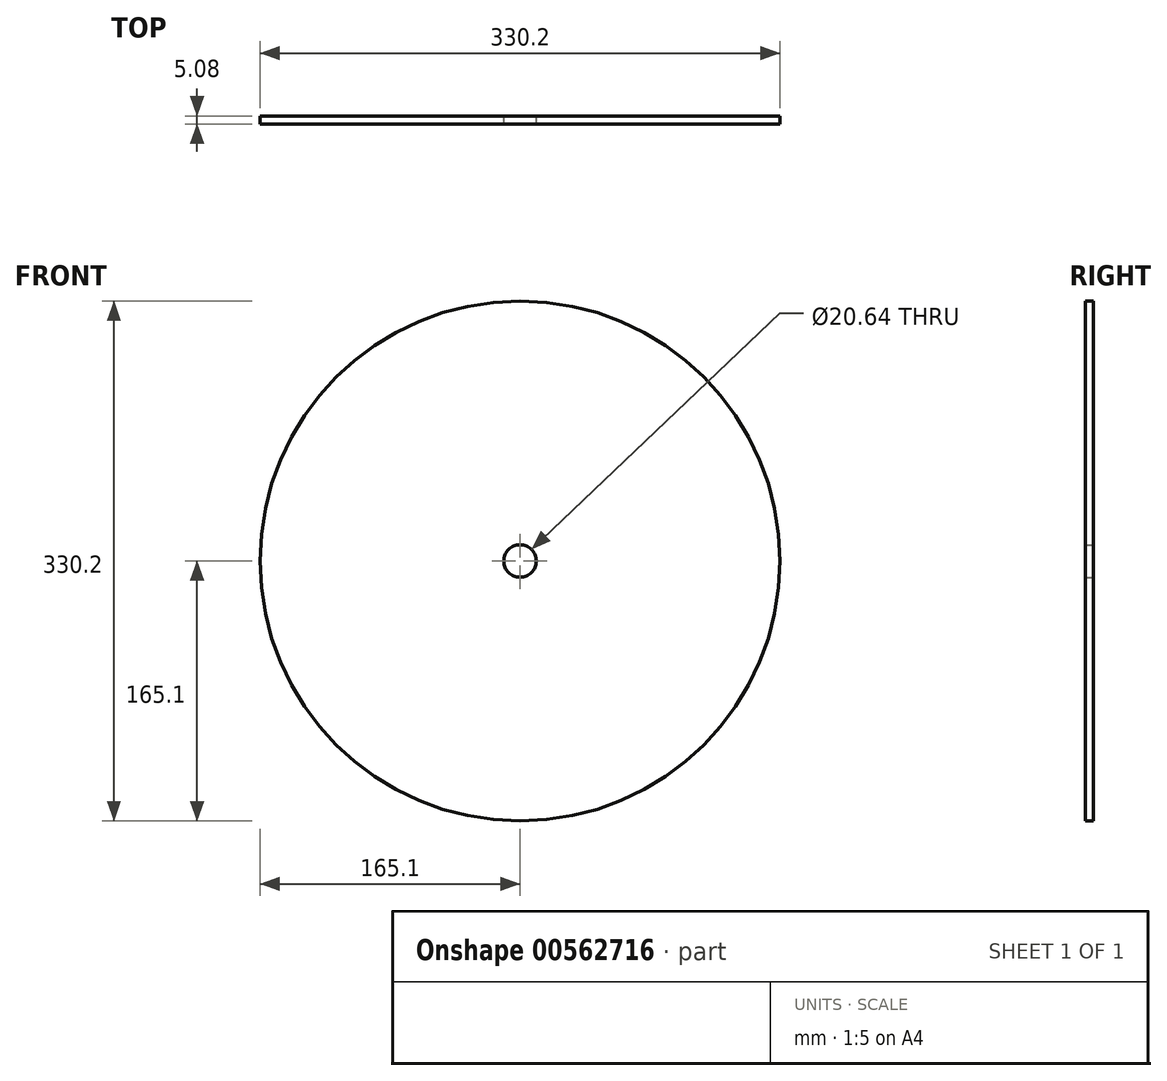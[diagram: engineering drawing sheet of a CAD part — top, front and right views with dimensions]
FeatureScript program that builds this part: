
annotation { "Feature Type Name" : "Feature", "Feature Type Description" : "" }
export const myFeature = defineFeature(function(context is Context, id is Id, definition is map)
    precondition{}
    {
        {
            var Q0;
            Q0=qCreatedBy(makeId("Front.planeOp"),FACE);
            var sketch = newSketch(context, id + "F0", { "sketchPlane" : qUnion([Q0])});
            skCircle(sketch, "E0", {"center": v(0, 0) * mm, "radius": 165.1 * mm});
            skCircle(sketch, "E1", {"center": v(0, 0) * mm, "radius": 10.32 * mm});
            skSolve(sketch);
        }
        {
            var Q0;
            Q0=makeQuery(id+"F0.imprint","IMPRINT",FACE,{"disambiguationData":[TD([[makeQuery(id+"F0.imprint","IMPRINT",EDGE,{"derivedFrom":sQuery(id+"F0.wireOp",EDGE,"E0")}),1.0]])]});
            extrude(context, id + "F1", {"entities" : qUnion([Q0]), "depth" : 5.08 * mm, "offsetDistance" : 25.4 * mm});
        }
    });
